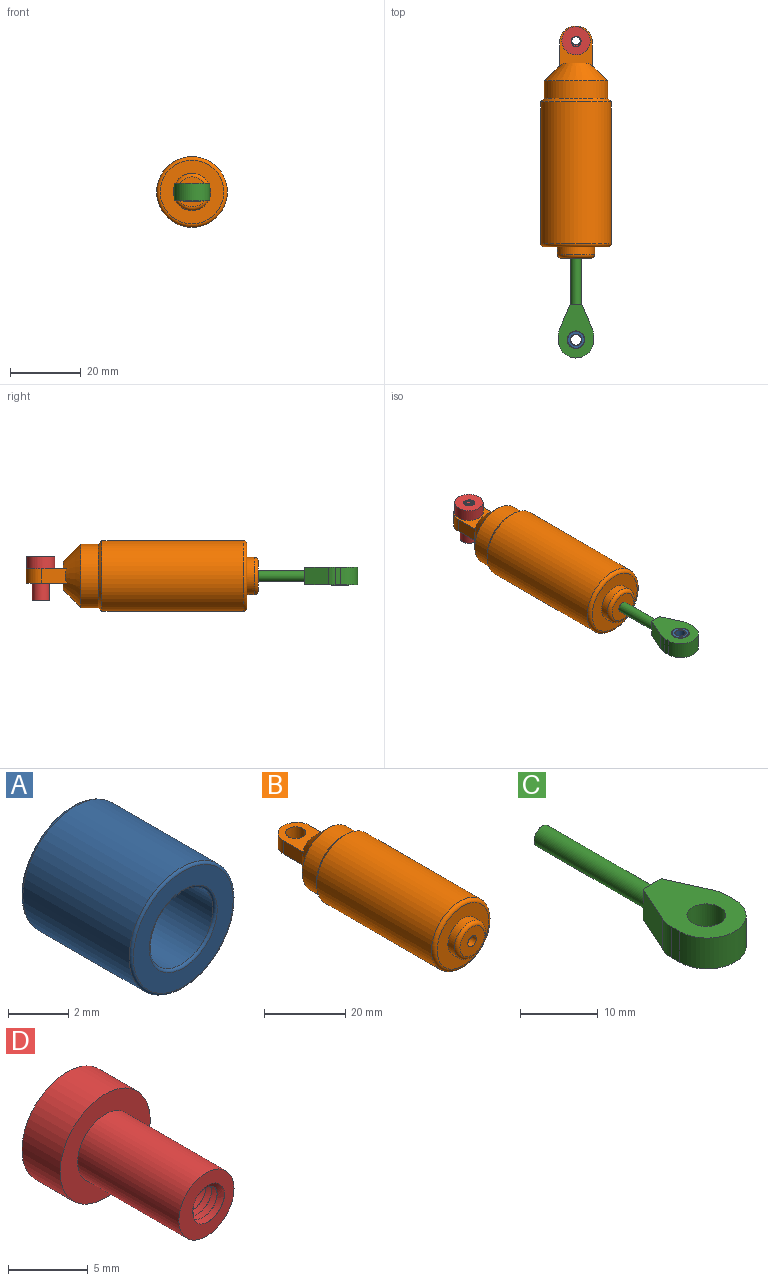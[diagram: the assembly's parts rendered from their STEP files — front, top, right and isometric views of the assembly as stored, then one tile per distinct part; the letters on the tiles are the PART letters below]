
ASSEMBLY  parts=4 mates=3
PART A: 8 faces, bbox 5.3x5.2x5.3 mm
  f0: cylinder r=1.5mm len=5mm, axis (0,1,0), area 47.1mm2, adj f4,f6
  f1: cylinder r=2.45mm len=5mm, axis (0,1,0), area 77mm2, adj f5,f7
  f2: plane 4.7x4.7mm, normal (0,-1,0), area 9.3mm2, adj f6,f7
  f3: plane 4.7x4.7mm, normal (0,1,0), area 9.3mm2, adj f4,f5
  f4: torus R=1.6mm, axis (0,-1,0), area 1.5mm2, adj f0,f3
  f5: torus R=2.35mm, axis (0,-1,0), area 2.4mm2, adj f1,f3
  f6: torus R=1.6mm, axis (0,-1,0), area 1.5mm2, adj f0,f2
  f7: torus R=2.35mm, axis (0,-1,0), area 2.4mm2, adj f1,f2
PART B: 21 faces, bbox 21.7x65.8x21.7 mm
  f0: plane 6.93x2mm, normal (0,1,0), area 9.8mm2, adj f7,f16
  f1: cylinder r=9mm len=18mm, axis (0,1,0), area 282.7mm2, adj f15,f16
  f2: plane 6.93x2mm, normal (0,1,0), area 9.8mm2, adj f9,f16
  f3: cylinder r=10mm len=40mm, axis (0,1,0), area 2513.3mm2, adj f15,f17
  f4: plane 18x18mm, normal (0,-1,0), area 167.9mm2, adj f5,f17
  f5: cylinder r=5.25mm len=10.5mm, axis (0,1,0), area 72.6mm2, adj f4,f18
  f6: plane 8.5x8.5mm, normal (0,-1,0), area 49.7mm2, adj f18,f19
  f7: plane 11.58x9.26mm, normal (0,0,1), area 69.4mm2, adj f0,f8,f10,f11,f12,f13,f14,f16
  f8: plane 7.02x4mm, normal (1,0,0), area 27mm2, adj f7,f9,f13,f16
  f9: plane 11.58x9.26mm, normal (0,0,-1), area 69.4mm2, adj f2,f8,f10,f11,f12,f13,f14,f16
  f10: plane 7.02x4mm, normal (-1,0,0), area 27mm2, adj f7,f9,f14,f16
  f11: plane 4x0.2mm, normal (0,1,0), area 0.8mm2, adj f7,f9,f13,f14
  f12: cylinder r=2.5mm len=5mm, axis (0,0,1), area 62.8mm2, adj f7,f9
  f13: cylinder r=4.5mm len=4.5mm, axis (0,0,1), area 28.3mm2, adj f7,f8,f9,f11
  f14: cylinder r=4.5mm len=4.5mm, axis (0,0,-1), area 28.3mm2, adj f7,f9,f10,f11
  f15: cone r=11mm half-angle=45deg, axis (0,-1,0), area 84.4mm2, adj f1,f3
  f16: cone r=9mm half-angle=45deg, axis (0,-1,0), area 279.9mm2, adj f0,f1,f2,f7,f8,f9,f10
  f17: torus R=9mm, axis (0,-1,0), area 95.1mm2, adj f3,f4
  f18: torus R=4.25mm, axis (0,-1,0), area 48.2mm2, adj f5,f6
  f19: cylinder r=1.5mm len=25mm, axis (0,-1,0), area 235.6mm2, adj f6,f20
  f20: plane 3x3mm, normal (0,-1,0), area 7.1mm2, adj f19
PART C: 13 faces, bbox 10x35x4.9 mm
  f0: plane 15x10mm, normal (0,0,1), area 94.2mm2, adj f1,f5,f6,f7,f8,f9,f10,f11
  f1: plane 4.85x3.26mm, normal (0,1,0), area 8.7mm2, adj f0,f2,f3,f9,f10
  f2: plane 15x10mm, normal (0,0,-1), area 94.2mm2, adj f1,f5,f6,f7,f8,f9,f10,f11
  f3: cylinder r=1.5mm len=20mm, axis (0,1,0), area 188.5mm2, adj f1,f4
  f4: plane 3x3mm, normal (0,1,0), area 7.1mm2, adj f3
  f5: plane 4.85x1.43mm, normal (-1,0,0), area 6.9mm2, adj f0,f2,f8,f12
  f6: plane 4.85x1.43mm, normal (1,0,0), area 6.9mm2, adj f0,f2,f8,f11
  f7: cylinder r=2.5mm len=5mm, axis (0,0,1), area 76.2mm2, adj f0,f2
  f8: cylinder r=5mm len=10mm, axis (0,0,-1), area 76.2mm2, adj f0,f2,f5,f6
  f9: plane 6.52x4.85mm, normal (0.91,0.41,0), area 34.7mm2, adj f0,f1,f2,f11
  f10: plane 6.52x4.85mm, normal (-0.91,0.41,0), area 34.7mm2, adj f0,f1,f2,f12
  f11: cylinder r=5mm len=4.85mm, axis (0,0,-1), area 10.2mm2, adj f0,f2,f6,f9
  f12: cylinder r=5mm len=4.85mm, axis (0,0,-1), area 10.2mm2, adj f0,f2,f5,f10
PART D: 8 faces, bbox 8.4x13.3x8.4 mm
  f0: plane 8.35x8.35mm, normal (0,1,0), area 44mm2, adj f1,f3,f6,f7
  f1: cylinder r=1.2mm len=12.4mm, axis (0,1,0), area 2mm2, adj f0,f2,f6,f7
  f2: plane 5.24x5.24mm, normal (0,-1,0), area 12.6mm2, adj f1,f5,f6,f7
  f3: cylinder r=4mm len=8mm, axis (0,1,0), area 85.5mm2, adj f0,f4
  f4: plane 8x8mm, normal (0,-1,0), area 31.4mm2, adj f3,f5
  f5: cylinder r=2.45mm len=9mm, axis (0,1,0), area 138.5mm2, adj f2,f4
  f6: bspline ~12.91x3.75mm, area 107.9mm2, adj f0,f1,f2,f7
  f7: bspline ~13x3.75mm, area 108mm2, adj f0,f1,f2,f6
PLACE A rot(axis=(-1,0,0),90deg) t=(27.99,-77.49,2.59)mm
PLACE B t=(27.99,0.81,5.26)mm
PLACE C t=(27.99,-47.64,5.26)mm
PLACE D rot(axis=(1,0,0),90deg) t=(27.99,7.11,10.66)mm
MATE fastened A.f0 <-> C.f7  axis (0,0,-1) through (27.99,-77.49,7.69)mm
MATE revolute D.f1 <-> B.f12  axis (0,0,-1) through (27.99,7.11,7.26)mm
MATE cylindrical C.f3 <-> B.f1  axis (0,1,0) through (27.99,-47.64,5.26)mm
